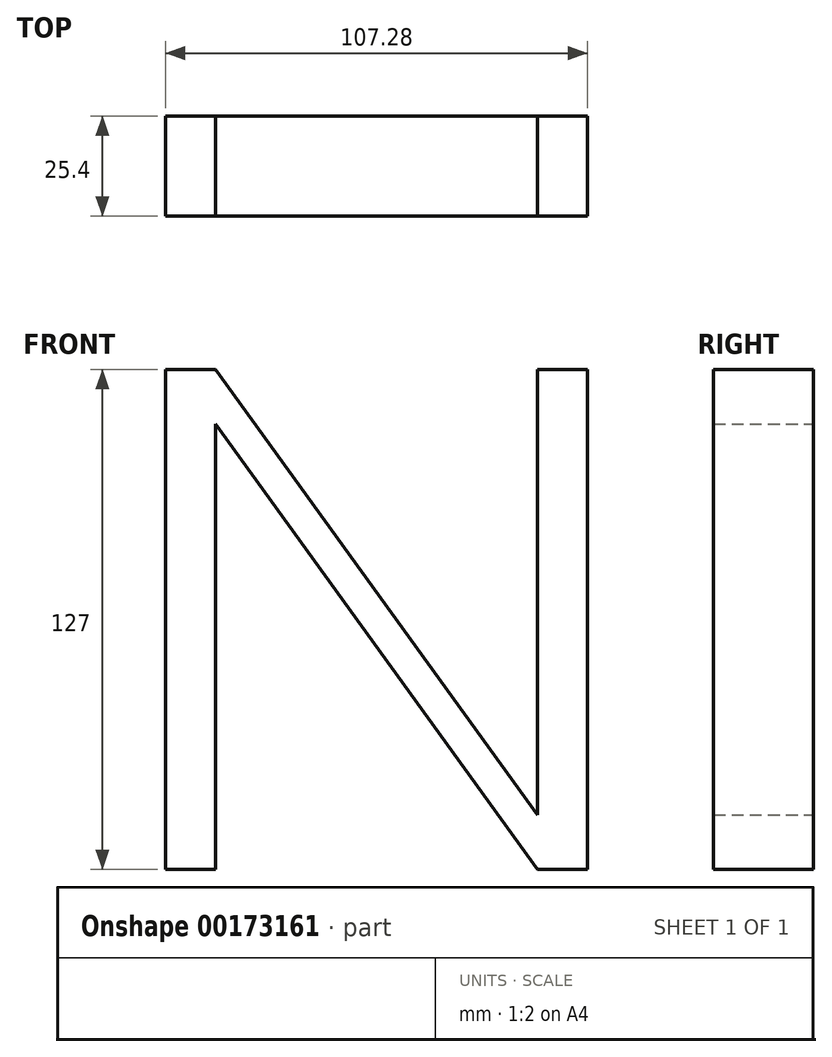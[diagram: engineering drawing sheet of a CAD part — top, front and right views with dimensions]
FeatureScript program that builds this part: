
annotation { "Feature Type Name" : "Feature", "Feature Type Description" : "" }
export const myFeature = defineFeature(function(context is Context, id is Id, definition is map)
    precondition{}
    {
        {
            var Q0;
            Q0=qCreatedBy(makeId("Front.planeOp"),FACE);
            var sketch = newSketch(context, id + "F0", { "sketchPlane" : qUnion([Q0])});
            skLineSegment(sketch, "E0", {"start": v(-66.08, 70.64) * mm, "end": v(-66.08, -56.36) * mm});
            skLineSegment(sketch, "E1", {"start": v(-66.08, -56.36) * mm, "end": v(-53.38, -56.36) * mm});
            skLineSegment(sketch, "E2", {"start": v(-66.08, 70.64) * mm, "end": v(-53.38, 70.64) * mm});
            skLineSegment(sketch, "E3", {"start": v(-53.38, -56.36) * mm, "end": v(-53.38, -0.89) * mm});
            skLineSegment(sketch, "E4", {"start": v(-53.38, 70.64) * mm, "end": v(38.5, -56.36) * mm});
            skLineSegment(sketch, "E5", {"start": v(-53.38, -0.89) * mm, "end": v(-53.38, 56.82) * mm});
            skLineSegment(sketch, "E6", {"start": v(-53.38, 56.82) * mm, "end": v(28.5, -56.36) * mm});
            skLineSegment(sketch, "E7", {"start": v(28.5, -42.55) * mm, "end": v(28.5, 70.64) * mm});
            skLineSegment(sketch, "E8", {"start": v(28.5, 70.64) * mm, "end": v(41.2, 70.64) * mm});
            skLineSegment(sketch, "E9", {"start": v(41.2, 70.64) * mm, "end": v(41.2, -56.36) * mm});
            skLineSegment(sketch, "E10", {"start": v(28.5, -56.36) * mm, "end": v(41.2, -56.36) * mm});
            skSolve(sketch);
        }
        {
            var Q0;
            {var subQ1=sQuery(id+"F0.wireOp",EDGE,"E7");Q0=makeQuery(id+"F0.imprint","IMPRINT",FACE,{"disambiguationData":[TD([[makeQuery(id+"F0.imprint","IMPRINT",EDGE,{"derivedFrom":subQ1}),-1.0]])]});}
            extrude(context, id + "F1", {"entities" : qUnion([Q0]), "endBound" : BoundingType.SYMMETRIC, "depth" : 25.4 * mm});
        }
        {
            var Q0;
            Q0=makeQuery(id+"F0.imprint","IMPRINT",FACE,{"disambiguationData":[TD([[makeQuery(id+"F0.imprint","IMPRINT",EDGE,{"derivedFrom":sQuery(id+"F0.wireOp",EDGE,"E0")}),1.0]])]});
            extrude(context, id + "F2", {"entities" : qUnion([Q0]), "operationType" : NewBodyOperationType.ADD, "endBound" : BoundingType.SYMMETRIC, "depth" : 25.4 * mm});
        }
    });
